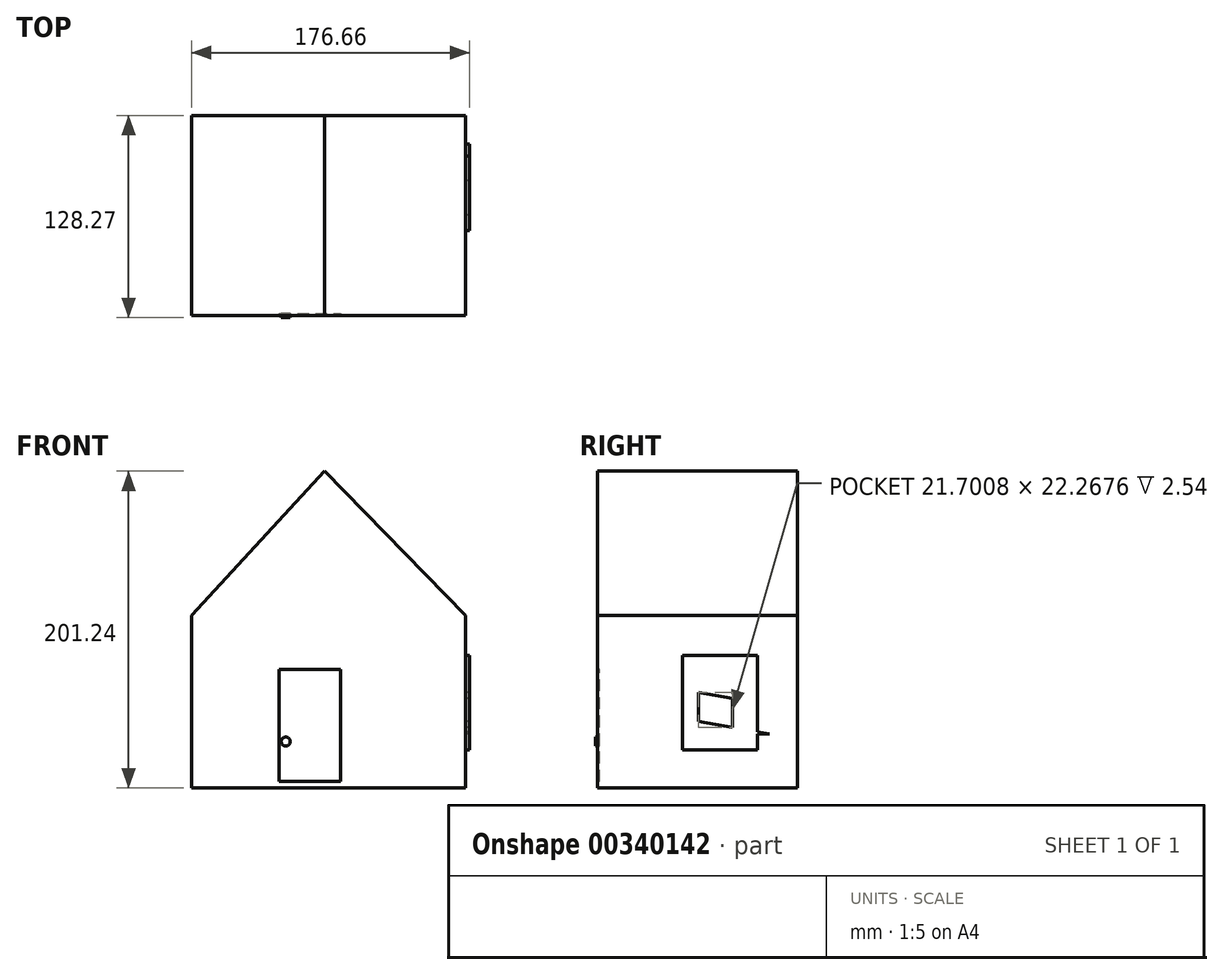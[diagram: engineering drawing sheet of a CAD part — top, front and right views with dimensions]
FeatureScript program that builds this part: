
annotation { "Feature Type Name" : "Feature", "Feature Type Description" : "" }
export const myFeature = defineFeature(function(context is Context, id is Id, definition is map)
    precondition{}
    {
        {
            var Q0;
            Q0=qCreatedBy(makeId("Front.planeOp"),FACE);
            var sketch = newSketch(context, id + "F0", { "sketchPlane" : qUnion([Q0])});
            skLineSegment(sketch, "E0.bottom", {"start": v(0, 0) * mm, "end": v(-174.12, 0) * mm});
            skLineSegment(sketch, "E0.top", {"start": v(0, -109.55) * mm, "end": v(-174.12, -109.55) * mm});
            skLineSegment(sketch, "E0.left", {"start": v(0, 0) * mm, "end": v(0, -109.55) * mm});
            skLineSegment(sketch, "E0.right", {"start": v(-174.12, 0) * mm, "end": v(-174.12, -109.55) * mm});
            skLineSegment(sketch, "E1", {"start": v(-174.12, 0) * mm, "end": v(-89.62, 91.69) * mm});
            skLineSegment(sketch, "E2", {"start": v(0, 0) * mm, "end": v(-89.62, 91.69) * mm});
            skSolve(sketch);
        }
        {
            var Q0;
            Q0 = qSketchRegion(id + "F0", true);
            extrude(context, id + "F1", {"entities" : qUnion([Q0]), "depth" : 127 * mm});
        }
        {
            var Q0;
            Q0=makeQuery(id+"F1.opExtrude","CAP_FACE",FACE,{"disambiguationData":[OSD([sQuery(id+"F0.wireOp",EDGE,"E0.top"),sQuery(id+"F0.wireOp",EDGE,"E0.left"),sQuery(id+"F0.wireOp",EDGE,"E0.right"),sQuery(id+"F0.wireOp",EDGE,"E1"),sQuery(id+"F0.wireOp",EDGE,"E2")])],"isStart":false});
            var sketch = newSketch(context, id + "F2", { "sketchPlane" : qUnion([Q0])});
            skLineSegment(sketch, "E3.bottom", {"start": v(-118.44, -105.5) * mm, "end": v(-79.54, -105.5) * mm});
            skLineSegment(sketch, "E3.top", {"start": v(-118.44, -34.3) * mm, "end": v(-79.54, -34.3) * mm});
            skLineSegment(sketch, "E3.left", {"start": v(-118.44, -105.5) * mm, "end": v(-118.44, -34.3) * mm});
            skLineSegment(sketch, "E3.right", {"start": v(-79.54, -105.5) * mm, "end": v(-79.54, -34.3) * mm});
            skSolve(sketch);
        }
        {
            var Q0;
            Q0 = qSketchRegion(id + "F2", true);
            extrude(context, id + "F3", {"entities" : qUnion([Q0]), "operationType" : NewBodyOperationType.REMOVE, "oppositeDirection" : true, "depth" : 1.27 * mm});
        }
        {
            var Q0;
            Q0=makeQuery(id+"F3.boolean.opBoolean","COPY",FACE,{"derivedFrom":makeQuery(id+"F3.opExtrude","CAP_FACE",FACE,{"disambiguationData":[OSD([sQuery(id+"F2.wireOp",EDGE,"E3.bottom"),sQuery(id+"F2.wireOp",EDGE,"E3.top"),sQuery(id+"F2.wireOp",EDGE,"E3.left"),sQuery(id+"F2.wireOp",EDGE,"E3.right")])],"isStart":false})});
            var sketch = newSketch(context, id + "F4", { "sketchPlane" : qUnion([Q0])});
            skCircle(sketch, "E4", {"center": v(-114.26, -80.12) * mm, "radius": 2.87 * mm});
            skSolve(sketch);
        }
        {
            var Q0;
            Q0 = qSketchRegion(id + "F4", true);
            extrude(context, id + "F5", {"entities" : qUnion([Q0]), "operationType" : NewBodyOperationType.ADD, "depth" : 2.54 * mm});
        }
        {
            var Q0;
            Q0=makeQuery(id+"F1.opExtrude","SWEPT_FACE",FACE,{"disambiguationData":[OSD([sQuery(id+"F0.wireOp",EDGE,"E0.left")])]});
            var sketch = newSketch(context, id + "F6", { "sketchPlane" : qUnion([Q0])});
            skLineSegment(sketch, "E5.bottom", {"start": v(-73.11, -25.43) * mm, "end": v(-25.54, -25.43) * mm});
            skLineSegment(sketch, "E5.top", {"start": v(-73.11, -85.39) * mm, "end": v(-25.54, -85.39) * mm});
            skLineSegment(sketch, "E5.left", {"start": v(-73.11, -25.43) * mm, "end": v(-73.11, -85.39) * mm});
            skLineSegment(sketch, "E5.right", {"start": v(-25.54, -25.43) * mm, "end": v(-25.54, -85.39) * mm});
            skLineSegment(sketch, "E6", {"start": v(-63.1, -25.43) * mm, "end": v(-63.1, -85.39) * mm});
            skPoint(sketch, "E6.endSnap0", {"position": v(-49.32, -85.39) * mm});
            skLineSegment(sketch, "E7", {"start": v(-41.4, -25.43) * mm, "end": v(-41.4, -85.39) * mm});
            skLineSegment(sketch, "E8", {"start": v(-25.54, -55.41) * mm, "end": v(-73.11, -47.05) * mm});
            skLineSegment(sketch, "E9", {"start": v(-63.1, -48.8) * mm, "end": v(-71.97, -47.25) * mm});
            skPoint(sketch, "E9.startSnap0", {"position": v(-63.1, -55.41) * mm});
            skLineSegment(sketch, "E10", {"start": v(-73.11, -65.52) * mm, "end": v(-18.03, -75.17) * mm});
            skLineSegment(sketch, "E11", {"start": v(-18.03, -75.17) * mm, "end": v(-25.54, -75.17) * mm});
            skSolve(sketch);
        }
        {
            var Q0;
            Q0 = qSketchRegion(id + "F6", true);
            extrude(context, id + "F7", {"entities" : qUnion([Q0]), "operationType" : NewBodyOperationType.ADD, "depth" : 2.54 * mm});
        }
    });
